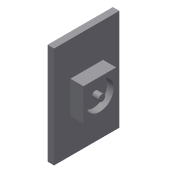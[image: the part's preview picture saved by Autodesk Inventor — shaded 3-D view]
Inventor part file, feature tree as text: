
AUTODESK INVENTOR PART (.ipt)
format: ipt  version: 2019.4 (Build 234330000, 330)  size: 98,816 bytes
history: native  units: mm
features: extrude x4, sketch x4, projected_geometry x1
ambient origin geometry x8: Origin, YZ Plane, XZ Plane, XY Plane, X Axis, Y Axis, Z Axis, Center Point
bodies: Solid1 (feature_tree)
feature tree (9):
  extrude  "Extrusion1"  Depth=10.0mm
  extrude  "Extrusion2"  Depth=5.0mm
  extrude  "Extrusion3"  Depth=2.0mm TaperAngle=0.0deg
  extrude  "Extrusion4"  Depth=15.0mm TaperAngle=0.0deg
  sketch  "Sketch1"  dims[d0=15.5mm d1=10.0mm]
  sketch  "Sketch2"  dims[d2=1.0mm d3=0.0mm d4=5.0mm]
  sketch  "Sketch3"  dims[d5=5.0mm d6=2.0mm d7=0.0mm]
  projected_geometry  "Projected Loop1"
  sketch  "Sketch4"  dims[d8=1.0mm d9=0.0mm d10=15.0mm d11=0.0mm]
